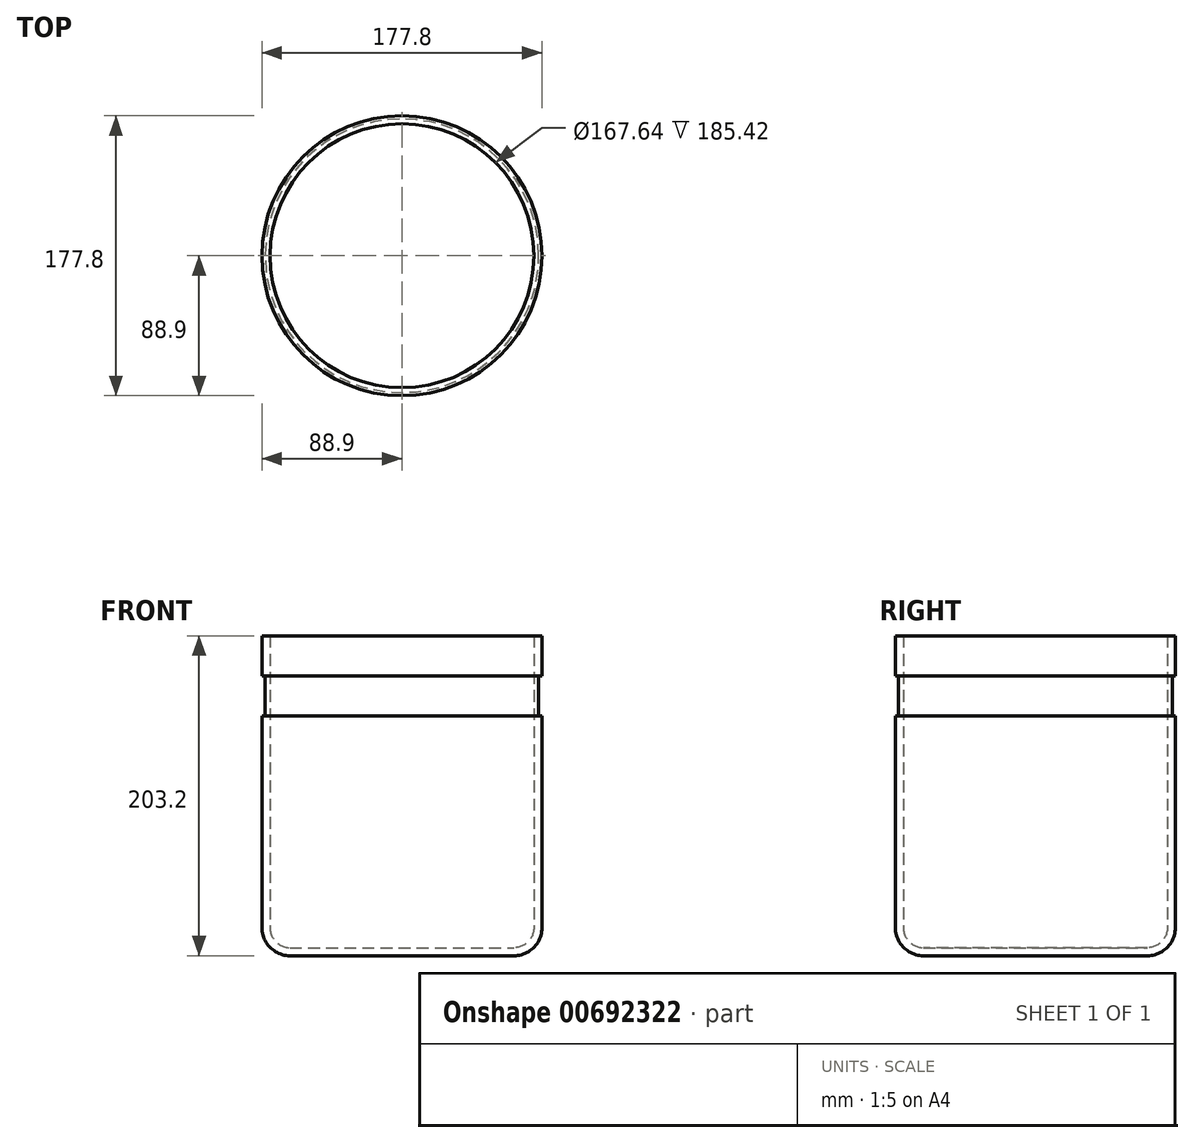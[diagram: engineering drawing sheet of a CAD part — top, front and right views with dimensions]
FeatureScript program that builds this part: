
annotation { "Feature Type Name" : "Feature", "Feature Type Description" : "" }
export const myFeature = defineFeature(function(context is Context, id is Id, definition is map)
    precondition{}
    {
        {
            var Q0;
            Q0=qCreatedBy(makeId("Front.planeOp"),FACE);
            var sketch = newSketch(context, id + "F0", { "sketchPlane" : qUnion([Q0])});
            skLineSegment(sketch, "E0.bottom", {"start": v(0, 0) * mm, "end": v(71.12, 0) * mm});
            skLineSegment(sketch, "E0.top", {"start": v(0, 5.08) * mm, "end": v(71.12, 5.08) * mm});
            skLineSegment(sketch, "E0.left", {"start": v(0, 0) * mm, "end": v(0, 5.08) * mm});
            skLineSegment(sketch, "E1.top", {"start": v(88.9, 203.2) * mm, "end": v(83.82, 203.2) * mm});
            skLineSegment(sketch, "E1.left", {"start": v(88.9, 17.78) * mm, "end": v(88.9, 203.2) * mm});
            skLineSegment(sketch, "E1.right", {"start": v(83.82, 17.78) * mm, "end": v(83.82, 203.2) * mm});
            skPoint(sketch, "E2.visualSharp", {"position": v(88.9, 0) * mm});
            skArc(sketch, "E2.filletArc", {"start": v(71.12, 0) * mm, "mid": v(83.7, 5.2) * mm, "end": v(88.9, 17.78) * mm});
            skLineSegment(sketch, "E3", {"start": v(0, 5.08) * mm, "end": v(0, 37.5) * mm, "construction": true});
            skPoint(sketch, "E4.visualSharp", {"position": v(83.82, 5.08) * mm});
            skArc(sketch, "E4.filletArc", {"start": v(71.12, 5.08) * mm, "mid": v(80.1, 8.8) * mm, "end": v(83.82, 17.78) * mm});
            skSolve(sketch);
        }
        {
            var Q0;
            Q0 = qSketchRegion(id + "F0", true);
            var Q1;
            Q1=sQuery(id+"F0.wireOp",EDGE,"E3");
            revolve(context, id + "F1", {"entities" : qUnion([Q0]), "axis" : qUnion([Q1]), "revolveType" : RevolveType.FULL});
        }
        {
            var Q0;
            Q0=qCreatedBy(makeId("Front.planeOp"),FACE);
            var sketch = newSketch(context, id + "F2", { "sketchPlane" : qUnion([Q0])});
            skLineSegment(sketch, "E5.bottom", {"start": v(88.9, 177.8) * mm, "end": v(86.87, 177.8) * mm});
            skLineSegment(sketch, "E5.top", {"start": v(88.9, 152.4) * mm, "end": v(86.87, 152.4) * mm});
            skLineSegment(sketch, "E5.left", {"start": v(88.9, 177.8) * mm, "end": v(88.9, 152.4) * mm});
            skLineSegment(sketch, "E5.right", {"start": v(86.87, 177.8) * mm, "end": v(86.87, 152.4) * mm});
            skLineSegment(sketch, "E6.0", {"start": v(88.9, 203.2) * mm, "end": v(-88.9, 203.2) * mm, "construction": true});
            skSolve(sketch);
        }
        {
            var Q0;
            Q0 = qSketchRegion(id + "F2", true);
            var Q1;
            Q1=makeQuery(id+"F1.opRevolve","SWEPT_FACE",FACE,{"disambiguationData":[OSD([sQuery(id+"F0.wireOp",EDGE,"E1.left")])]});
            revolve(context, id + "F3", {"operationType" : NewBodyOperationType.REMOVE, "entities" : qUnion([Q0]), "axis" : qUnion([Q1]), "revolveType" : RevolveType.FULL, "oppositeDirection" : true});
        }
    });
